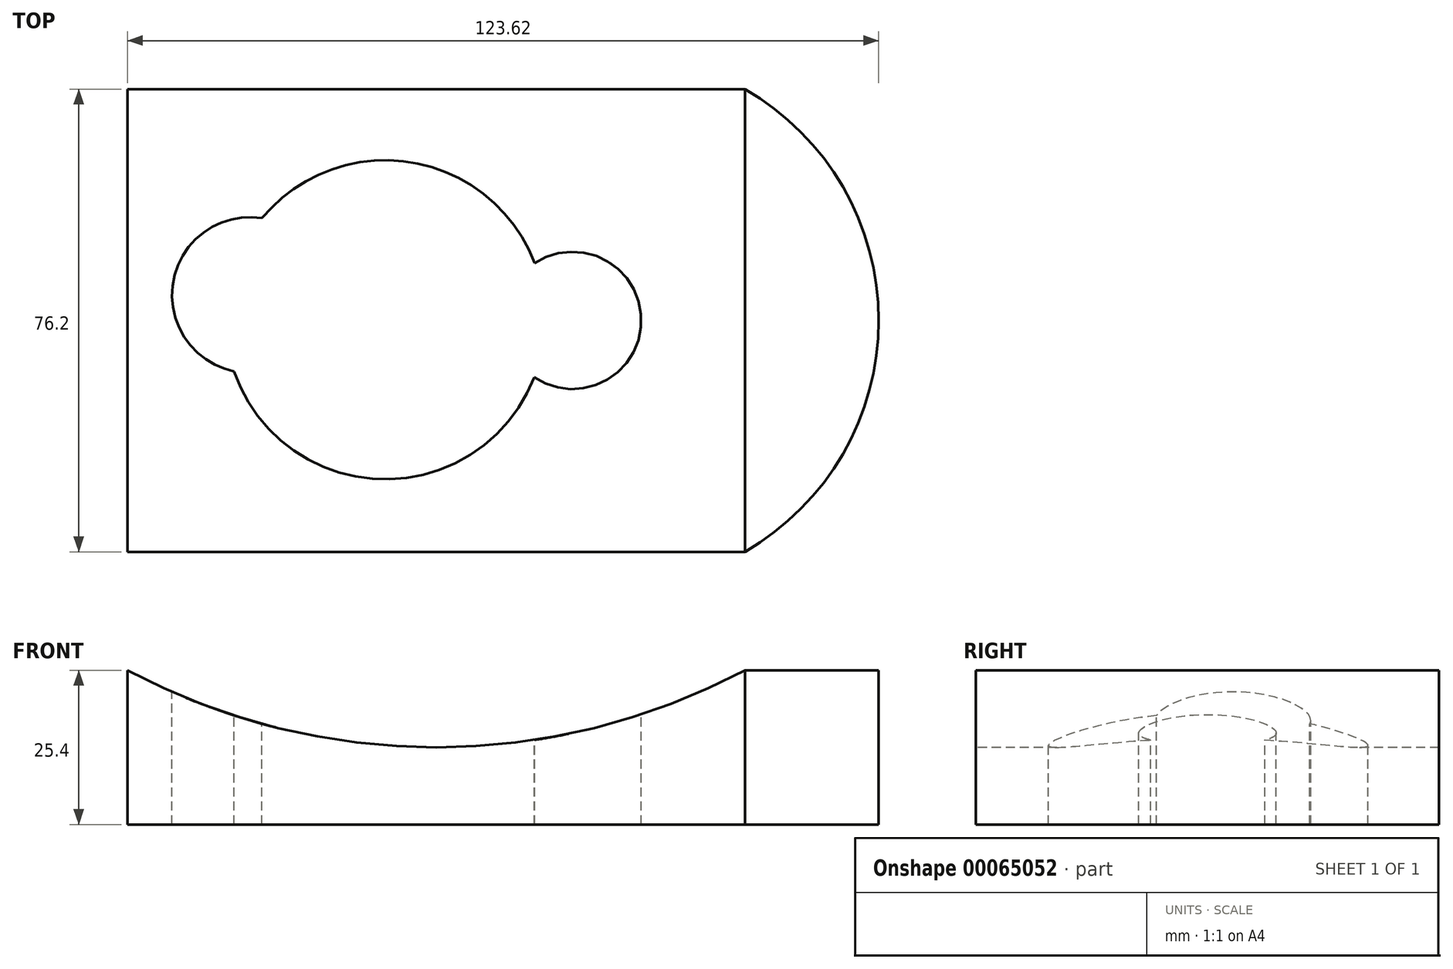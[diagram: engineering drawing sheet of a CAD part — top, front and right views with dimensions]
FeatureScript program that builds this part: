
annotation { "Feature Type Name" : "Feature", "Feature Type Description" : "" }
export const myFeature = defineFeature(function(context is Context, id is Id, definition is map)
    precondition{}
    {
        {
            var Q0;
            Q0=qCreatedBy(makeId("Top.planeOp"),FACE);
            var sketch = newSketch(context, id + "F0", { "sketchPlane" : qUnion([Q0])});
            skLineSegment(sketch, "E0.bottom", {"start": v(-58.55, 20.29) * mm, "end": v(68.45, 20.29) * mm});
            skLineSegment(sketch, "E0.top", {"start": v(-58.55, -55.91) * mm, "end": v(68.45, -55.91) * mm});
            skLineSegment(sketch, "E0.left", {"start": v(-58.55, 20.29) * mm, "end": v(-58.55, -55.91) * mm});
            skLineSegment(sketch, "E0.right", {"start": v(68.45, 20.29) * mm, "end": v(68.45, -55.91) * mm});
            skSolve(sketch);
        }
        {
            var Q0;
            Q0=makeQuery(id+"F0.imprint","IMPRINT",FACE,{"disambiguationData":[TD([[makeQuery(id+"F0.imprint","IMPRINT",EDGE,{"derivedFrom":sQuery(id+"F0.wireOp",EDGE,"E0.bottom")}),-1.0]])]});
            extrude(context, id + "F1", {"entities" : qUnion([Q0]), "depth" : 25.4 * mm});
        }
        {
            var Q0;
            Q0=makeQuery(id+"F1.opExtrude","CAP_FACE",FACE,{"disambiguationData":[OSD([sQuery(id+"F0.wireOp",EDGE,"E0.bottom"),sQuery(id+"F0.wireOp",EDGE,"E0.top"),sQuery(id+"F0.wireOp",EDGE,"E0.left"),sQuery(id+"F0.wireOp",EDGE,"E0.right")])],"isStart":false});
            var sketch = newSketch(context, id + "F2", { "sketchPlane" : qUnion([Q0])});
            skLineSegment(sketch, "E1", {"start": v(68.45, -55.91) * mm, "end": v(43.05, -55.91) * mm});
            skLineSegment(sketch, "E2", {"start": v(68.45, -17.81) * mm, "end": v(68.45, -55.91) * mm});
            skLineSegment(sketch, "E3", {"start": v(43.05, 20.29) * mm, "end": v(68.45, 20.29) * mm});
            skLineSegment(sketch, "E4", {"start": v(68.45, -17.81) * mm, "end": v(68.45, 20.29) * mm});
            skArc(sketch, "E5", {"start": v(43.05, -55.91) * mm, "mid": v(65.07, -17.81) * mm, "end": v(43.05, 20.29) * mm});
            skSolve(sketch);
        }
        {
            var Q0;
            Q0=makeQuery(id+"F2.imprint","IMPRINT",FACE,{"disambiguationData":[TD([[makeQuery(id+"F2.imprint","IMPRINT",EDGE,{"derivedFrom":sQuery(id+"F2.wireOp",EDGE,"E2")}),-1.0]])]});
            var Q1;
            Q1 = qSketchRegion(id + "F4", true);
            extrude(context, id + "F3", {"entities" : qUnion([Q0, Q1]), "operationType" : NewBodyOperationType.REMOVE, "oppositeDirection" : true, "depth" : 25.4 * mm});
        }
        {
            var Q0;
            Q0=makeQuery(id+"F1.opExtrude","CAP_FACE",FACE,{"disambiguationData":[OSD([sQuery(id+"F0.wireOp",EDGE,"E0.bottom"),sQuery(id+"F0.wireOp",EDGE,"E0.top"),sQuery(id+"F0.wireOp",EDGE,"E0.left"),sQuery(id+"F0.wireOp",EDGE,"E0.right")])],"isStart":false});
            var sketch = newSketch(context, id + "F4", { "sketchPlane" : qUnion([Q0])});
            skCircle(sketch, "E6", {"center": v(14.7, -17.81) * mm, "radius": 11.3 * mm});
            skCircle(sketch, "E7", {"center": v(-38.38, -13.65) * mm, "radius": 12.82 * mm});
            skCircle(sketch, "E8", {"center": v(-16.13, -17.7) * mm, "radius": 26.28 * mm});
            skSolve(sketch);
        }
        {
            var Q0;
            Q0 = qSketchRegion(id + "F4", true);
            extrude(context, id + "F5", {"entities" : qUnion([Q0]), "operationType" : NewBodyOperationType.REMOVE, "oppositeDirection" : true, "depth" : 25.4 * mm});
        }
        {
            var Q0;
            Q0=makeQuery(id+"F1.opExtrude","SWEPT_FACE",FACE,{"disambiguationData":[OSD([sQuery(id+"F0.wireOp",EDGE,"E0.top")])]});
            var sketch = newSketch(context, id + "F6", { "sketchPlane" : qUnion([Q0])});
            skArc(sketch, "E9", {"start": v(-58.55, 25.4) * mm, "mid": v(-7.75, 12.7) * mm, "end": v(43.05, 25.4) * mm});
            skSolve(sketch);
        }
        {
            var Q0;
            Q0=makeQuery(id+"F6.imprint","IMPRINT",FACE,{"disambiguationData":[TD([[makeQuery(id+"F6.imprint","IMPRINT",EDGE,{"derivedFrom":sQuery(id+"F6.wireOp",EDGE,"E9")}),1.0]])]});
            extrude(context, id + "F7", {"entities" : qUnion([Q0]), "operationType" : NewBodyOperationType.REMOVE, "oppositeDirection" : true, "depth" : 94.23 * mm});
        }
    });
